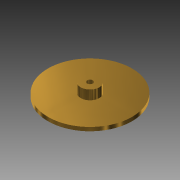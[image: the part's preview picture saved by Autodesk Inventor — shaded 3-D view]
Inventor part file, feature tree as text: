
AUTODESK INVENTOR PART (.ipt)
format: ipt  version: 2015 (Build 190159000, 159)  size: 110,592 bytes
history: native  units: mm
features: extrude x4, sketch x4, other x1
ambient origin geometry x8: Origin, YZ Plane, XZ Plane, XY Plane, X Axis, Y Axis, Z Axis, Center Point
bodies: Body1 (feature_tree)
feature tree (9):
  other  "ソリッド1"
  extrude  "押し出し1"  Depth=45.0mm
  extrude  "押し出し2"  Depth=2.0mm TaperAngle=0.0deg
  extrude  "押し出し3"  Depth=10.0mm
  extrude  "押し出し4"  Depth=5.0mm TaperAngle=0.0deg
  sketch  "スケッチ1"
  sketch  "スケッチ2"
  sketch  "スケッチ3"
  sketch  "スケッチ4"
